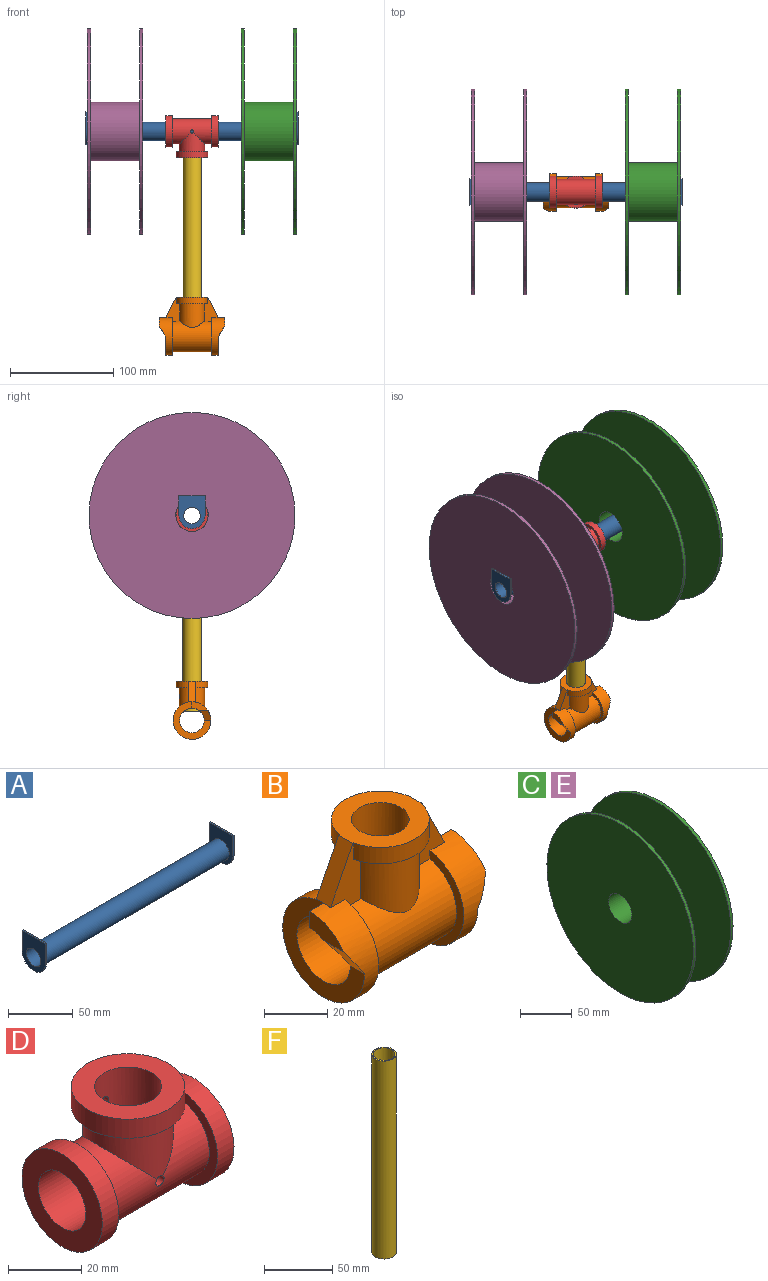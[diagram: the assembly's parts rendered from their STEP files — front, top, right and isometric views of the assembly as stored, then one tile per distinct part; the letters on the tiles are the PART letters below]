
ASSEMBLY  parts=6 mates=5
PART A: 14 faces, bbox 206.4x25.4x31.8 mm
  f0: cylinder r=7.95mm len=206.38mm, axis (-1,0,0), area 10309mm2, adj f6,f12
  f1: cylinder r=8.99mm len=203.2mm, axis (-1,0,0), area 11480mm2, adj f7,f13
  f2: plane 19.05x1.59mm, normal (0,1,0), area 30.2mm2, adj f3,f5,f6,f7
  f3: plane 25.4x1.59mm, normal (0,0,1), area 40.3mm2, adj f2,f4,f6,f7
  f4: plane 19.05x1.59mm, normal (0,-1,0), area 30.2mm2, adj f3,f5,f6,f7
  f5: cylinder r=12.7mm len=25.4mm, axis (-1,0,0), area 63.3mm2, adj f2,f4,f6,f7
  f6: plane 31.75x25.4mm, normal (1,0,0), area 538.7mm2, adj f0,f2,f3,f4,f5
  f7: plane 31.75x25.4mm, normal (-1,0,0), area 483.2mm2, adj f1,f2,f3,f4,f5
  f8: plane 25.4x1.59mm, normal (0,0,1), area 40.3mm2, adj f9,f11,f12,f13
  f9: plane 19.05x1.59mm, normal (0,1,0), area 30.2mm2, adj f8,f10,f12,f13
  f10: cylinder r=12.7mm len=25.4mm, axis (1,0,0), area 63.3mm2, adj f9,f11,f12,f13
  f11: plane 19.05x1.59mm, normal (0,-1,0), area 30.2mm2, adj f8,f10,f12,f13
  f12: plane 31.75x25.4mm, normal (-1,0,0), area 538.7mm2, adj f0,f8,f9,f10,f11
  f13: plane 31.75x25.4mm, normal (1,0,0), area 483.2mm2, adj f1,f8,f9,f10,f11
PART B: 31 faces, bbox 63.5x36.6x56.4 mm
  f0: plane 36.58x36.58mm, normal (-1,0,0), area 452.5mm2, adj f7,f13,f18,f20,f27,f30
  f1: plane 36.58x36.58mm, normal (1,0,0), area 452.5mm2, adj f7,f10,f21,f23,f25,f29
  f2: plane 3.18x0.28mm, normal (1,0,0), area 0.3mm2, adj f10,f21,f22
  f3: cylinder r=12.32mm len=23.81mm, axis (0,0,-1), area 633.1mm2, adj f5,f6,f20,f23,f24
  f4: cylinder r=15.49mm len=30.33mm, axis (0,0,1), area 268.5mm2, adj f5,f17,f20,f23
  f5: plane 30.33x12.32mm, normal (0,0,-1), area 118.4mm2, adj f3,f4,f20,f23
  f6: cylinder r=15.11mm len=38.1mm, axis (-1,0,0), area 2997.5mm2, adj f3,f8,f11,f12,f19,f20,f22,f23
  f7: cylinder r=11.94mm len=63.5mm, axis (-1,0,0), area 3690.9mm2, adj f0,f1,f16,f25,f26,f27,f28,f29
  f8: cylinder r=12.32mm len=23.81mm, axis (0,0,-1), area 651.1mm2, adj f6,f15,f19,f22
  f9: plane 3.18x0.28mm, normal (-1,0,0), area 0.3mm2, adj f13,f18,f19
  f10: cylinder r=18.29mm len=36.58mm, axis (1,0,0), area 838.4mm2, adj f1,f2,f11,f22,f23,f25,f26,f29
  f11: plane 36.58x36.3mm, normal (-1,0,0), area 312.9mm2, adj f6,f10,f22,f23
  f12: plane 36.58x36.3mm, normal (1,0,0), area 312.9mm2, adj f6,f13,f19,f20
  f13: cylinder r=18.29mm len=36.58mm, axis (1,0,0), area 838.4mm2, adj f0,f9,f12,f19,f20,f27,f28,f30
  f14: cylinder r=15.49mm len=30.33mm, axis (0,0,1), area 268.5mm2, adj f15,f17,f19,f22
  f15: plane 30.33x12.32mm, normal (0,0,-1), area 118.4mm2, adj f8,f14,f19,f22
  f16: cylinder r=9.14mm len=30.43mm, axis (0,0,-1), area 1600.9mm2, adj f7,f17,f24
  f17: plane 30.99x30.99mm, normal (0,0,1), area 492.9mm2, adj f4,f14,f16,f18,f19,f20,f21,f22
  f18: plane 19.81x9.91mm, normal (-0.89,0,0.45), area 140.7mm2, adj f0,f9,f17,f19,f20
  f19: plane 23.32x13.5mm, normal (0,-1,0), area 175.4mm2, adj f6,f8,f9,f12,f13,f14,f15,f17
  f20: plane 23.32x13.5mm, normal (0,1,0), area 175.4mm2, adj f0,f3,f4,f5,f6,f12,f13,f17
  f21: plane 19.81x9.91mm, normal (0.89,0,0.45), area 140.7mm2, adj f1,f2,f17,f22,f23
  f22: plane 23.32x13.5mm, normal (0,-1,0), area 175.4mm2, adj f2,f6,f8,f10,f11,f14,f15,f17
  f23: plane 23.32x13.5mm, normal (0,1,0), area 175.4mm2, adj f1,f3,f4,f5,f6,f10,f11,f17
  f24: cylinder r=2.38mm len=4.76mm, axis (0,-1,0), area 48.1mm2, adj f3,f16
  f25: plane 6.35x6.35mm, normal (0,1,0), area 40.3mm2, adj f1,f7,f10,f26
  f26: plane 15.21x8.13mm, normal (1,0,0), area 79.4mm2, adj f7,f10,f25,f29
  f27: plane 6.35x6.35mm, normal (0,1,0), area 40.3mm2, adj f0,f7,f13,f28
  f28: plane 15.21x8.13mm, normal (-1,0,0), area 79.4mm2, adj f7,f13,f27,f30
  f29: plane 12.02x10.16mm, normal (0.85,0,-0.53), area 84.2mm2, adj f1,f7,f10,f26
  f30: plane 12.02x10.16mm, normal (-0.85,0,-0.53), area 84.2mm2, adj f0,f7,f13,f28
PART C: 8 faces, bbox 54x200x200 mm
  f0: cylinder r=100.01mm len=200.03mm, axis (-1,0,0), area 1995.2mm2, adj f1,f2
  f1: plane 200.03x200.03mm, normal (1,0,0), area 28858.6mm2, adj f0,f6
  f2: plane 200.03x200.03mm, normal (-1,0,0), area 30632.1mm2, adj f0,f7
  f3: cylinder r=100.01mm len=200.03mm, axis (-1,0,0), area 1995.2mm2, adj f4,f5
  f4: plane 200.03x200.03mm, normal (1,0,0), area 30632.1mm2, adj f3,f7
  f5: plane 200.03x200.03mm, normal (-1,0,0), area 28858.6mm2, adj f3,f6
  f6: cylinder r=28.57mm len=57.15mm, axis (-1,0,0), area 8550.7mm2, adj f1,f5
  f7: cylinder r=15.88mm len=53.98mm, axis (-1,0,0), area 5383.8mm2, adj f2,f4
PART D: 15 faces, bbox 50.8x31x40.9 mm
  f0: cylinder r=12.32mm len=38.1mm, axis (-1,0,0), area 2336.1mm2, adj f2,f7,f8,f14
  f1: cylinder r=9.14mm len=50.8mm, axis (-1,0,0), area 2578.2mm2, adj f3,f4,f5,f14
  f2: cylinder r=12.32mm len=24.64mm, axis (0,0,-1), area 857.5mm2, adj f0,f11,f13,f14
  f3: cylinder r=9.14mm len=25.4mm, axis (0,0,-1), area 1114.9mm2, adj f1,f12,f13,f14
  f4: plane 30.99x30.99mm, normal (1,0,0), area 491.5mm2, adj f1,f6
  f5: plane 30.99x30.99mm, normal (-1,0,0), area 491.5mm2, adj f1,f9
  f6: cylinder r=15.49mm len=30.99mm, axis (1,0,0), area 618.2mm2, adj f4,f7
  f7: plane 30.99x30.99mm, normal (-1,0,0), area 277.4mm2, adj f0,f6
  f8: plane 30.99x30.99mm, normal (1,0,0), area 277.4mm2, adj f0,f9
  f9: cylinder r=15.49mm len=30.99mm, axis (1,0,0), area 618.2mm2, adj f5,f8
  f10: cylinder r=15.49mm len=30.99mm, axis (0,0,1), area 618.2mm2, adj f11,f12
  f11: plane 30.99x30.99mm, normal (0,0,-1), area 277.4mm2, adj f2,f10
  f12: plane 30.99x30.99mm, normal (0,0,1), area 491.5mm2, adj f3,f10
  f13: cylinder r=1.59mm len=3.31mm, axis (0,-1,0), area 31.8mm2, adj f2,f3
  f14: cylinder r=1.59mm len=3.31mm, axis (0,1,0), area 31.8mm2, adj f0,f1,f2,f3
PART E: same geometry as C
PART F: 4 faces, bbox 18x18x177.8 mm
  f0: cylinder r=7.95mm len=177.8mm, axis (0,0,1), area 8881.6mm2, adj f1,f2
  f1: plane 17.98x17.98mm, normal (0,0,-1), area 55.4mm2, adj f0,f3
  f2: plane 17.98x17.98mm, normal (0,0,1), area 55.4mm2, adj f0,f3
  f3: cylinder r=8.99mm len=177.8mm, axis (0,0,1), area 10045mm2, adj f1,f2
PLACE A t=(-68.5,8.2,150.75)mm
PLACE B t=(-68.5,8.2,-48.27)mm
PLACE C t=(-20.88,8.2,150.75)mm
PLACE D rot(axis=(0,1,0),180deg) t=(-68.5,8.2,150.75)mm
PLACE E t=(-170.1,8.2,150.75)mm
PLACE F t=(-68.5,8.2,-39.67)mm
MATE slider E.f7 <-> A.f0  axis (-1,0,0) through (-170.1,8.2,150.75)mm
MATE fastened F.f3 <-> D.f3  axis (0,0,1) through (-68.5,8.2,138.13)mm
MATE slider C.f7 <-> A.f0  axis (1,0,0) through (33.1,8.2,150.75)mm
MATE fastened D.f0 <-> A.f1  axis (1,0,0) through (-68.5,8.2,150.75)mm
MATE fastened B.f3 <-> F.f3  axis (0,0,-1) through (-68.5,8.2,-39.67)mm
